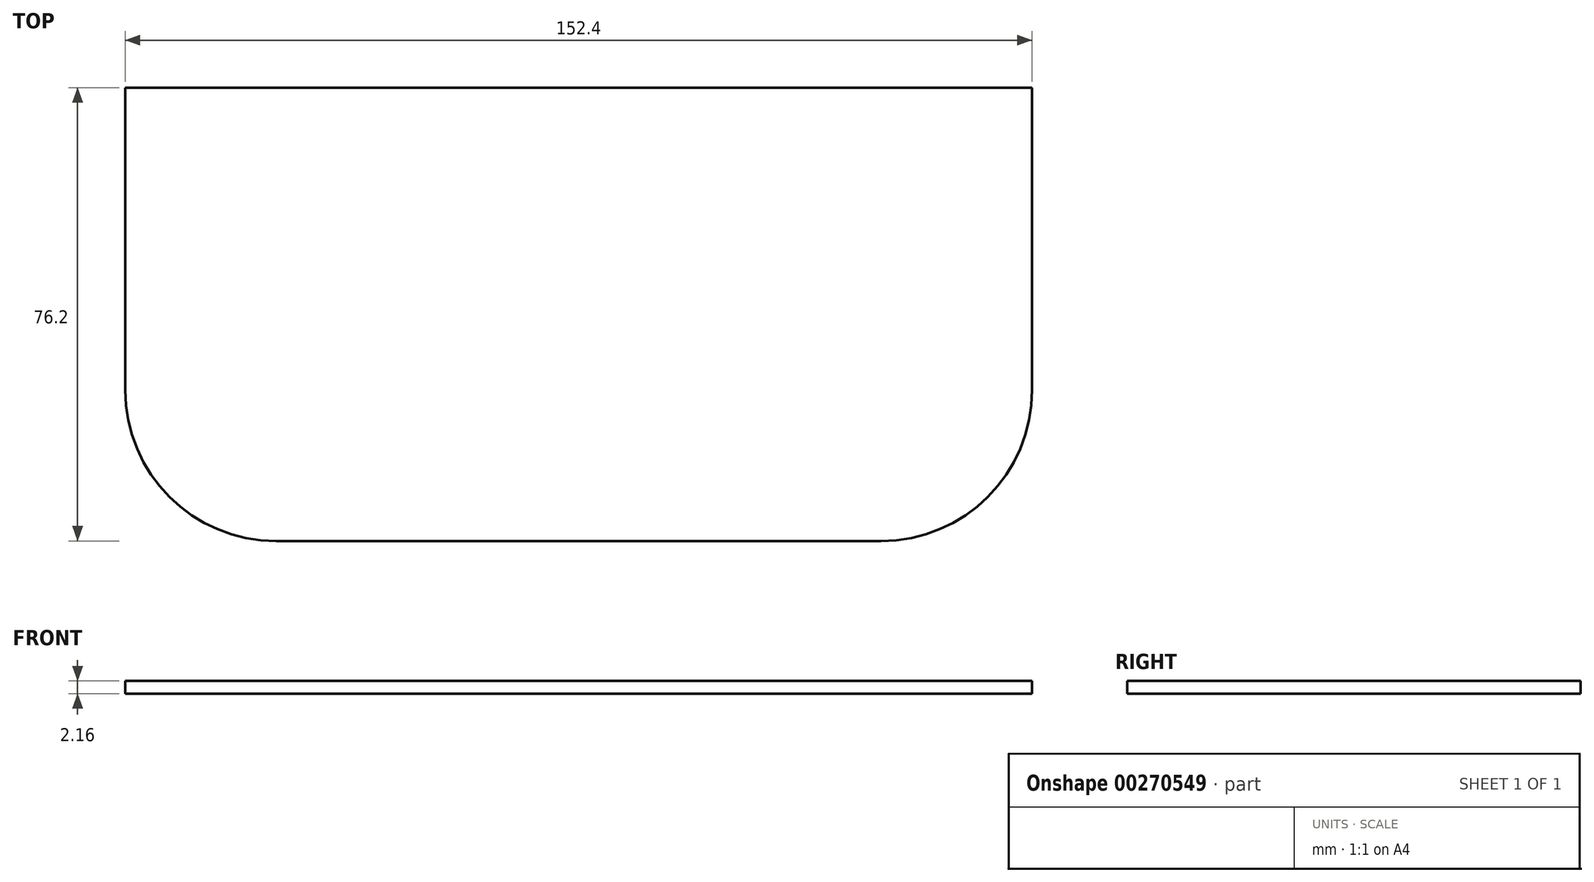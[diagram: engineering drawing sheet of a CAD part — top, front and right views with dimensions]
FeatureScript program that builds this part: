
annotation { "Feature Type Name" : "Feature", "Feature Type Description" : "" }
export const myFeature = defineFeature(function(context is Context, id is Id, definition is map)
    precondition{}
    {
        {
            var Q0;
            Q0=qCreatedBy(makeId("Top.planeOp"),FACE);
            var sketch = newSketch(context, id + "F0", { "sketchPlane" : qUnion([Q0])});
            skLineSegment(sketch, "E0.bottom", {"start": v(-76.72, -0.98) * mm, "end": v(75.68, -0.98) * mm});
            skLineSegment(sketch, "E0.top", {"start": v(-76.72, -77.18) * mm, "end": v(75.68, -77.18) * mm});
            skLineSegment(sketch, "E0.left", {"start": v(-76.72, -0.98) * mm, "end": v(-76.72, -77.18) * mm});
            skLineSegment(sketch, "E0.right", {"start": v(75.68, -0.98) * mm, "end": v(75.68, -77.18) * mm});
            skSolve(sketch);
        }
        {
            var Q0;
            Q0=makeQuery(id+"F0.imprint","IMPRINT",FACE,{"disambiguationData":[TD([[makeQuery(id+"F0.imprint","IMPRINT",EDGE,{"derivedFrom":sQuery(id+"F0.wireOp",EDGE,"E0.bottom")}),-1.0]])]});
            extrude(context, id + "F1", {"entities" : qUnion([Q0]), "depth" : 2.16 * mm});
        }
        {
            var Q0;
            Q0=makeQuery(id+"F1.opExtrude","SWEPT_EDGE",EDGE,{"disambiguationData":[OSD([sQuery(id+"F0.wireOp",EDGE,"E0.top"),sQuery(id+"F0.wireOp",EDGE,"E0.left")])]});
            var Q1;
            Q1=makeQuery(id+"F1.opExtrude","SWEPT_EDGE",EDGE,{"disambiguationData":[OSD([sQuery(id+"F0.wireOp",EDGE,"E0.top"),sQuery(id+"F0.wireOp",EDGE,"E0.right")])]});
            fillet(context, id + "F2", {"entities" : qUnion([Q0, Q1]), "radius" : 25.4 * mm, "tangentPropagation" : true, "allowEdgeOverflow" : false});
        }
    });
